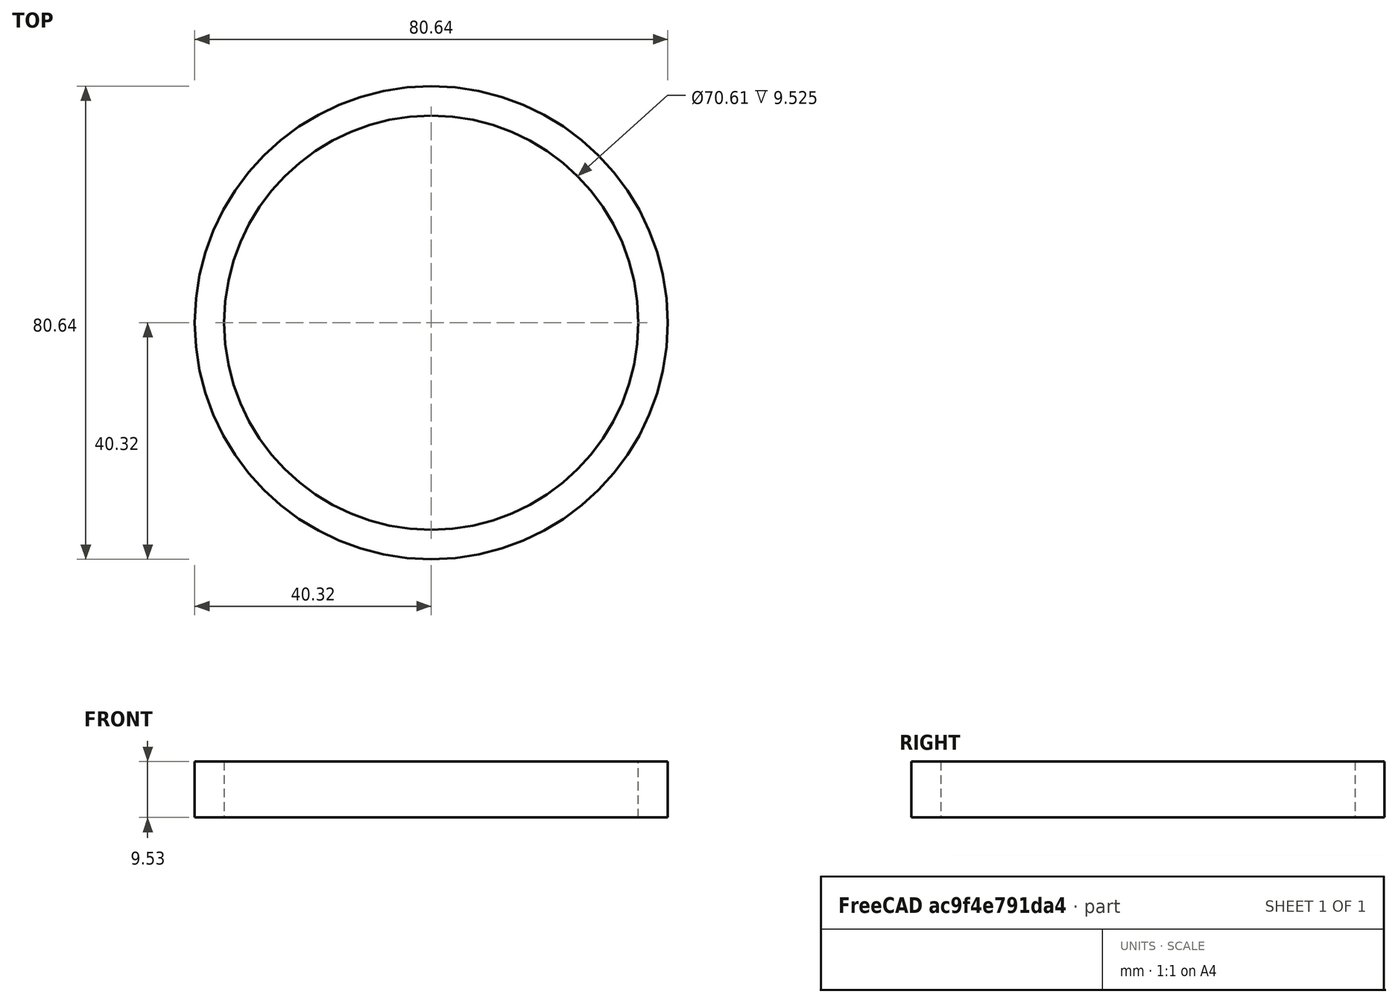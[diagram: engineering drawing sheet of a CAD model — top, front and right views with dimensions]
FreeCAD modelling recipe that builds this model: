
FCSTD DOCUMENT  (FreeCAD 0.21R33771 (Git))
Label: 3_175_OD_ring
License: All rights reserved
LicenseURL: http://en.wikipedia.org/wiki/All_rights_reserved
objects: Sketcher::SketchObject×1, PartDesign::Pad×1, PartDesign::Body×1
note: 4 computed .brp shape members not serialized (recipe doc carries the construction recipe); baked Part::Feature solids carry a one-line shape summary decoded from their .brp

FEATURE [Sketcher::SketchObject] Sketch
  FullyConstrained = true
  MapMode = 5
  Support = -> [XY_Plane]
  sketch-geometry (2):
    g0: Circle CenterX=0 CenterY=0 CenterZ=0 NormalX=0 NormalY=0 NormalZ=1 AngleXU=0 Radius=40.3225
    g1: Circle CenterX=0 CenterY=0 CenterZ=0 NormalX=0 NormalY=0 NormalZ=1 AngleXU=0 Radius=35.306
  constraints (4):
    c: Coincident(g0,g-1)
    c: Diameter(g0) = 80.645
    c: Coincident(g1,g0)
    c: Diameter(g1) = 70.612
FEATURE [PartDesign::Pad] Pad
  Direction = (0,0,1)
  Length = 9.525
  Length2 = 10
  Profile = -> Sketch
  ReferenceAxis = -> Sketch [N_Axis]
  Type = 0
FEATURE [PartDesign::Body] Body
  Group = -> [Sketch,Pad]
  Origin = -> Origin
  Tip = -> Pad
